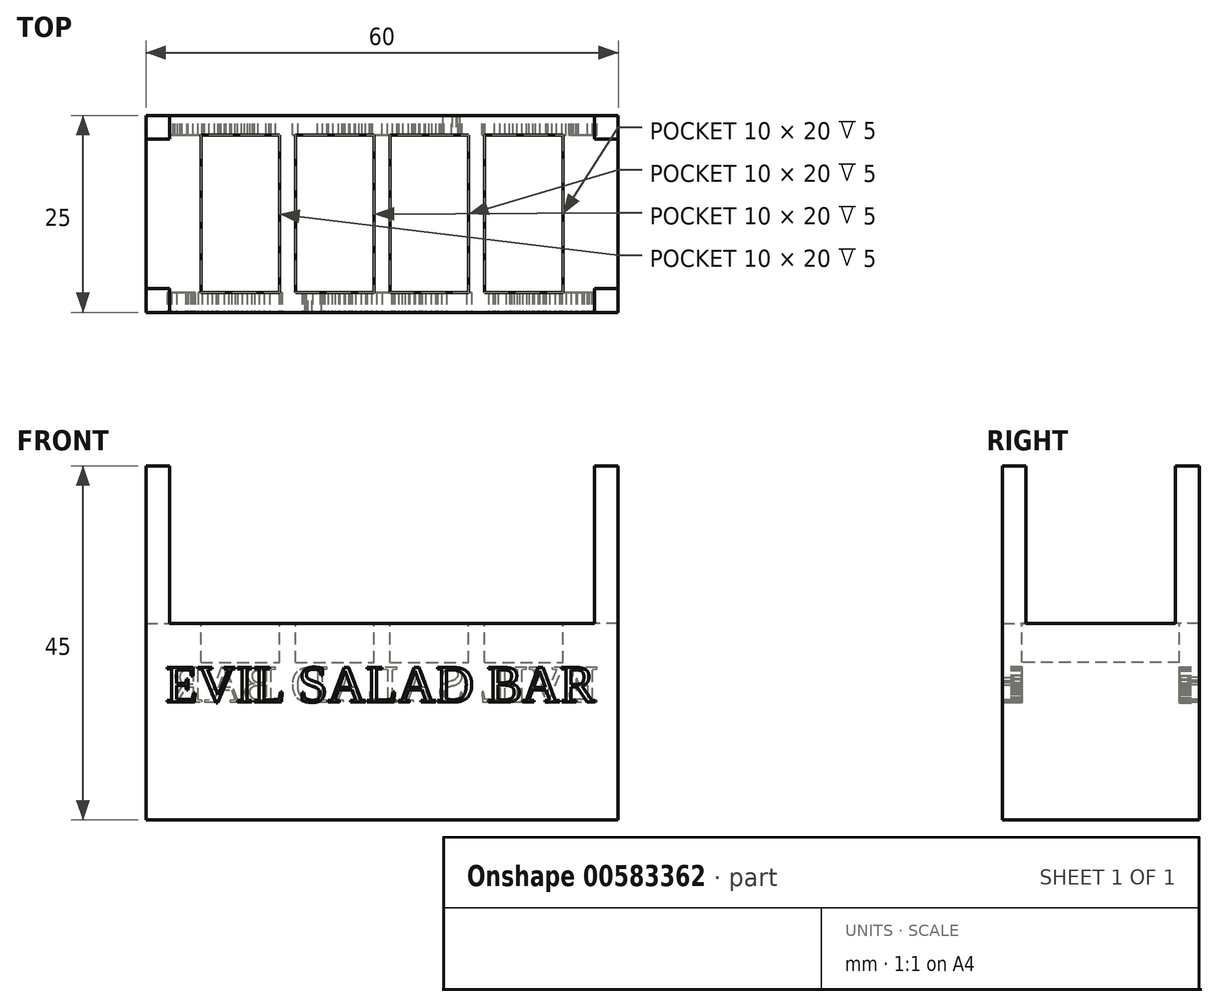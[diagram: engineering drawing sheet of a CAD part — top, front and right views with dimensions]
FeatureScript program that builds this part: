
annotation { "Feature Type Name" : "Feature", "Feature Type Description" : "" }
export const myFeature = defineFeature(function(context is Context, id is Id, definition is map)
    precondition{}
    {
        {
            var Q0;
            Q0=qCreatedBy(makeId("Top.planeOp"),FACE);
            var sketch = newSketch(context, id + "F0", { "sketchPlane" : qUnion([Q0])});
            skLineSegment(sketch, "E0.bottom", {"start": v(-58.32, 8.65) * mm, "end": v(1.68, 8.65) * mm});
            skLineSegment(sketch, "E0.top", {"start": v(-58.32, -16.35) * mm, "end": v(1.68, -16.35) * mm});
            skLineSegment(sketch, "E0.left", {"start": v(-58.32, 8.65) * mm, "end": v(-58.32, -16.35) * mm});
            skLineSegment(sketch, "E0.right", {"start": v(1.68, 8.65) * mm, "end": v(1.68, -16.35) * mm});
            skSolve(sketch);
        }
        {
            var Q0;
            Q0=makeQuery(id+"F0.imprint","IMPRINT",FACE,{"disambiguationData":[TD([[makeQuery(id+"F0.imprint","IMPRINT",EDGE,{"derivedFrom":sQuery(id+"F0.wireOp",EDGE,"E0.bottom")}),-1.0]])]});
            extrude(context, id + "F1", {"entities" : qUnion([Q0]), "depth" : 25 * mm, "offsetDistance" : 25 * mm});
        }
        {
            var Q0;
            Q0=makeQuery(id+"F1.opExtrude","CAP_FACE",FACE,{"disambiguationData":[OSD([sQuery(id+"F0.wireOp",EDGE,"E0.bottom"),sQuery(id+"F0.wireOp",EDGE,"E0.top"),sQuery(id+"F0.wireOp",EDGE,"E0.left"),sQuery(id+"F0.wireOp",EDGE,"E0.right")])],"isStart":false});
            var sketch = newSketch(context, id + "F2", { "sketchPlane" : qUnion([Q0])});
            skLineSegment(sketch, "E1.bottom", {"start": v(-51.32, 6.15) * mm, "end": v(-41.32, 6.15) * mm});
            skLineSegment(sketch, "E1.top", {"start": v(-51.32, -13.85) * mm, "end": v(-41.32, -13.85) * mm});
            skLineSegment(sketch, "E1.left", {"start": v(-51.32, 6.15) * mm, "end": v(-51.32, -13.85) * mm});
            skLineSegment(sketch, "E1.right", {"start": v(-41.32, 6.15) * mm, "end": v(-41.32, -13.85) * mm});
            skLineSegment(sketch, "E2.bottom", {"start": v(-39.32, 6.15) * mm, "end": v(-29.32, 6.15) * mm});
            skLineSegment(sketch, "E2.top", {"start": v(-39.32, -13.85) * mm, "end": v(-29.32, -13.85) * mm});
            skLineSegment(sketch, "E2.left", {"start": v(-39.32, 6.15) * mm, "end": v(-39.32, -13.85) * mm});
            skLineSegment(sketch, "E2.right", {"start": v(-29.32, 6.15) * mm, "end": v(-29.32, -13.85) * mm});
            skLineSegment(sketch, "E3.bottom", {"start": v(-27.32, 6.15) * mm, "end": v(-17.32, 6.15) * mm});
            skLineSegment(sketch, "E3.top", {"start": v(-27.32, -13.85) * mm, "end": v(-17.32, -13.85) * mm});
            skLineSegment(sketch, "E3.left", {"start": v(-27.32, 6.15) * mm, "end": v(-27.32, -13.85) * mm});
            skLineSegment(sketch, "E3.right", {"start": v(-17.32, 6.15) * mm, "end": v(-17.32, -13.85) * mm});
            skLineSegment(sketch, "E4.bottom", {"start": v(-15.32, 6.15) * mm, "end": v(-5.32, 6.15) * mm});
            skLineSegment(sketch, "E4.top", {"start": v(-15.32, -13.85) * mm, "end": v(-5.32, -13.85) * mm});
            skLineSegment(sketch, "E4.left", {"start": v(-15.32, 6.15) * mm, "end": v(-15.32, -13.85) * mm});
            skLineSegment(sketch, "E4.right", {"start": v(-5.32, 6.15) * mm, "end": v(-5.32, -13.85) * mm});
            skSolve(sketch);
        }
        {
            var Q0;
            Q0=makeQuery(id+"F2.imprint","IMPRINT",FACE,{"disambiguationData":[TD([[makeQuery(id+"F2.imprint","IMPRINT",EDGE,{"derivedFrom":sQuery(id+"F2.wireOp",EDGE,"E1.bottom")}),-1.0]])]});
            var Q1;
            Q1=makeQuery(id+"F2.imprint","IMPRINT",FACE,{"disambiguationData":[TD([[makeQuery(id+"F2.imprint","IMPRINT",EDGE,{"derivedFrom":sQuery(id+"F2.wireOp",EDGE,"E2.bottom")}),-1.0]])]});
            var Q2;
            Q2=makeQuery(id+"F2.imprint","IMPRINT",FACE,{"disambiguationData":[TD([[makeQuery(id+"F2.imprint","IMPRINT",EDGE,{"derivedFrom":sQuery(id+"F2.wireOp",EDGE,"E3.bottom")}),-1.0]])]});
            var Q3;
            Q3=makeQuery(id+"F2.imprint","IMPRINT",FACE,{"disambiguationData":[TD([[makeQuery(id+"F2.imprint","IMPRINT",EDGE,{"derivedFrom":sQuery(id+"F2.wireOp",EDGE,"E4.bottom")}),-1.0]])]});
            extrude(context, id + "F3", {"entities" : qUnion([Q0, Q1, Q2, Q3]), "operationType" : NewBodyOperationType.REMOVE, "oppositeDirection" : true, "depth" : 5 * mm, "offsetDistance" : 25 * mm});
        }
        {
            var Q0;
            Q0=makeQuery(id+"F1.opExtrude","CAP_FACE",FACE,{"disambiguationData":[OSD([sQuery(id+"F0.wireOp",EDGE,"E0.bottom"),sQuery(id+"F0.wireOp",EDGE,"E0.top"),sQuery(id+"F0.wireOp",EDGE,"E0.left"),sQuery(id+"F0.wireOp",EDGE,"E0.right")])],"isStart":false});
            var sketch = newSketch(context, id + "F4", { "sketchPlane" : qUnion([Q0])});
            skLineSegment(sketch, "E5.bottom", {"start": v(1.68, -16.35) * mm, "end": v(-1.32, -16.35) * mm});
            skLineSegment(sketch, "E5.top", {"start": v(1.68, -13.35) * mm, "end": v(-1.32, -13.35) * mm});
            skLineSegment(sketch, "E5.left", {"start": v(1.68, -16.35) * mm, "end": v(1.68, -13.35) * mm});
            skLineSegment(sketch, "E5.right", {"start": v(-1.32, -16.35) * mm, "end": v(-1.32, -13.35) * mm});
            skLineSegment(sketch, "E6.bottom", {"start": v(1.68, 8.65) * mm, "end": v(-1.32, 8.65) * mm});
            skLineSegment(sketch, "E6.top", {"start": v(1.68, 5.65) * mm, "end": v(-1.32, 5.65) * mm});
            skLineSegment(sketch, "E6.left", {"start": v(1.68, 8.65) * mm, "end": v(1.68, 5.65) * mm});
            skLineSegment(sketch, "E6.right", {"start": v(-1.32, 8.65) * mm, "end": v(-1.32, 5.65) * mm});
            skLineSegment(sketch, "E7.bottom", {"start": v(-58.32, 8.65) * mm, "end": v(-55.32, 8.65) * mm});
            skLineSegment(sketch, "E7.top", {"start": v(-58.32, 5.65) * mm, "end": v(-55.32, 5.65) * mm});
            skLineSegment(sketch, "E7.left", {"start": v(-58.32, 8.65) * mm, "end": v(-58.32, 5.65) * mm});
            skLineSegment(sketch, "E7.right", {"start": v(-55.32, 8.65) * mm, "end": v(-55.32, 5.65) * mm});
            skLineSegment(sketch, "E8.bottom", {"start": v(-58.32, -16.35) * mm, "end": v(-55.32, -16.35) * mm});
            skLineSegment(sketch, "E8.top", {"start": v(-58.32, -13.35) * mm, "end": v(-55.32, -13.35) * mm});
            skLineSegment(sketch, "E8.left", {"start": v(-58.32, -16.35) * mm, "end": v(-58.32, -13.35) * mm});
            skLineSegment(sketch, "E8.right", {"start": v(-55.32, -16.35) * mm, "end": v(-55.32, -13.35) * mm});
            skSolve(sketch);
        }
        {
            var Q0;
            Q0=qSketchRegion(id+"F4",true);
            extrude(context, id + "F5", {"entities" : qUnion([Q0]), "operationType" : NewBodyOperationType.ADD, "depth" : 20 * mm, "offsetDistance" : 25 * mm});
        }
        {
            var Q0;
            Q0=makeQuery(id+"F5.boolean.opBoolean","MERGE",FACE,{"derivedFrom":[makeQuery(id+"F1.opExtrude","SWEPT_FACE",FACE,{"disambiguationData":[OSD([sQuery(id+"F0.wireOp",EDGE,"E0.top")])]}),makeQuery(id+"F5.opExtrude","SWEPT_FACE",FACE,{"disambiguationData":[OSD([sQuery(id+"F4.wireOp",EDGE,"E5.bottom")])]}),makeQuery(id+"F5.opExtrude","SWEPT_FACE",FACE,{"disambiguationData":[OSD([sQuery(id+"F4.wireOp",EDGE,"E8.bottom")])]})]});
            var sketch = newSketch(context, id + "F6", { "sketchPlane" : qUnion([Q0])});
            skText(sketch, "E9", { "text": "EVIL SALAD BAR", "fontName": "Tinos-Regular.ttf"});
            const initialGuessF6  = {"E9": [-0.05582, 0.015, 1, 0, 0.00481]};
            skSetInitialGuess(sketch, initialGuessF6);
            skSolve(sketch);
        }
        {
            var Q0;
            Q0=qSketchRegion(id+"F6",true);
            extrude(context, id + "F7", {"entities" : qUnion([Q0]), "operationType" : NewBodyOperationType.REMOVE, "oppositeDirection" : true, "depth" : 2.5 * mm, "offsetDistance" : 25 * mm});
        }
        {
            var Q0;
            Q0=makeQuery(id+"F5.boolean.opBoolean","MERGE",FACE,{"derivedFrom":[makeQuery(id+"F1.opExtrude","SWEPT_FACE",FACE,{"disambiguationData":[OSD([sQuery(id+"F0.wireOp",EDGE,"E0.bottom")])]}),makeQuery(id+"F5.opExtrude","SWEPT_FACE",FACE,{"disambiguationData":[OSD([sQuery(id+"F4.wireOp",EDGE,"E6.bottom")])]}),makeQuery(id+"F5.opExtrude","SWEPT_FACE",FACE,{"disambiguationData":[OSD([sQuery(id+"F4.wireOp",EDGE,"E7.bottom")])]})]});
            var sketch = newSketch(context, id + "F8", { "sketchPlane" : qUnion([Q0])});
            skText(sketch, "E10", { "text": "EVIL SALAD BAR", "fontName": "Tinos-Regular.ttf"});
            const initialGuessF8  = {"E10": [0.00082, 0.015, 1, 0, 0.00481]};
            skSetInitialGuess(sketch, initialGuessF8);
            skSolve(sketch);
        }
        {
            var Q0;
            Q0=qSketchRegion(id+"F8",true);
            extrude(context, id + "F9", {"entities" : qUnion([Q0]), "operationType" : NewBodyOperationType.REMOVE, "oppositeDirection" : true, "depth" : 2.5 * mm, "offsetDistance" : 25 * mm});
        }
    });
